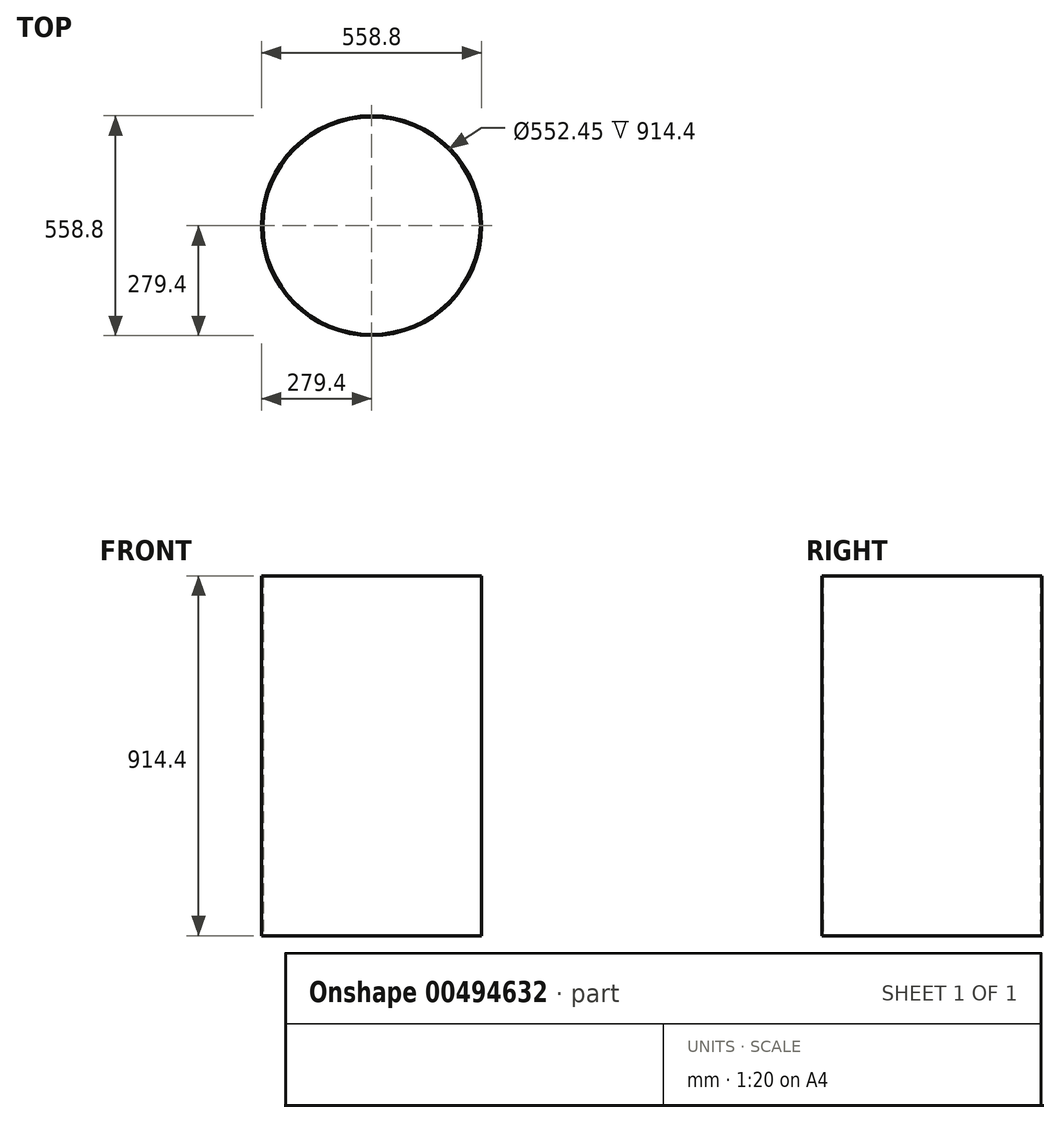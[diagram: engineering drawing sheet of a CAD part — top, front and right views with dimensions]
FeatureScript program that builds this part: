
annotation { "Feature Type Name" : "Feature", "Feature Type Description" : "" }
export const myFeature = defineFeature(function(context is Context, id is Id, definition is map)
    precondition{}
    {
        {
            var Q0;
            Q0=qCreatedBy(makeId("Top.planeOp"),FACE);
            var sketch = newSketch(context, id + "F0", { "sketchPlane" : qUnion([Q0])});
            skCircle(sketch, "E0", {"center": v(0, 0) * mm, "radius": 279.4 * mm});
            skCircle(sketch, "E1", {"center": v(0, 0) * mm, "radius": 276.23 * mm});
            skSolve(sketch);
        }
        {
            var Q0;
            Q0=sQuery(id+"F0.wireOp",EDGE,"E0");
            var Q1;
            Q1 = qConstructionFilter(qBodyType(qCreatedBy(id + "FlsjFQxeIRZsb6T_0" ,EDGE), BodyType.WIRE), ConstructionObject.NO);
            extrude(context, id + "F1", {"bodyType" : ToolBodyType.SURFACE, "surfaceEntities" : qUnion([Q0, Q1]), "depth" : 914.4 * mm});
        }
        {
            var Q0;
            Q0 = qSketchRegion(id + "F0", true);
            extrude(context, id + "F2", {"entities" : qUnion([Q0]), "depth" : 914.4 * mm});
        }
    });
